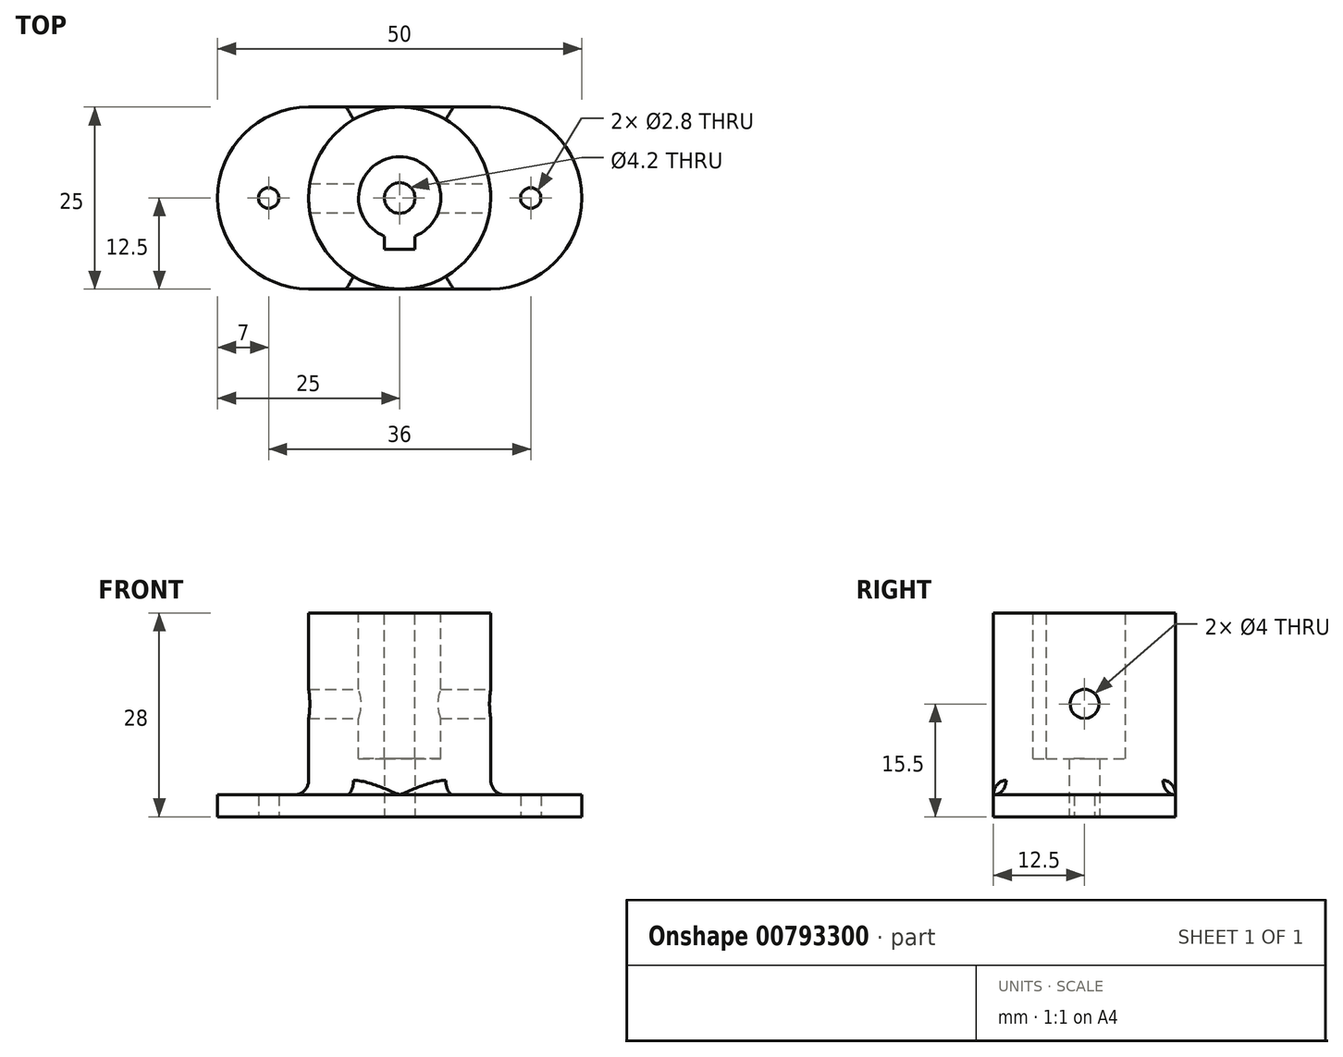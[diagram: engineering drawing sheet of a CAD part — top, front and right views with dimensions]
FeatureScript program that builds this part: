
annotation { "Feature Type Name" : "Feature", "Feature Type Description" : "" }
export const myFeature = defineFeature(function(context is Context, id is Id, definition is map)
    precondition{}
    {
        {
            var Q0;
            Q0=qCreatedBy(makeId("Top.planeOp"),FACE);
            var sketch = newSketch(context, id + "F0", { "sketchPlane" : qUnion([Q0])});
            skLineSegment(sketch, "E0.bottom", {"start": v(25, -12.5) * mm, "end": v(-25, -12.5) * mm});
            skLineSegment(sketch, "E0.top", {"start": v(25, 12.5) * mm, "end": v(-25, 12.5) * mm});
            skLineSegment(sketch, "E0.left", {"start": v(25, -12.5) * mm, "end": v(25, 12.5) * mm});
            skLineSegment(sketch, "E0.right", {"start": v(-25, -12.5) * mm, "end": v(-25, 12.5) * mm});
            skPoint(sketch, "E0.middle", {"position": v(0, 0) * mm});
            skCircle(sketch, "E1", {"center": v(-18, 0) * mm, "radius": 1.4 * mm});
            skCircle(sketch, "E2", {"center": v(18, 0) * mm, "radius": 1.4 * mm});
            skSolve(sketch);
        }
        {
            var Q0;
            Q0=qSketchRegion(id+"F0",true);
            extrude(context, id + "F1", {"entities" : qUnion([Q0]), "depth" : 3 * mm, "offsetDistance" : 25 * mm});
        }
        {
            var Q0;
            Q0=makeQuery(id+"F1.opExtrude","SWEPT_EDGE",EDGE,{"disambiguationData":[OSD([sQuery(id+"F0.wireOp",EDGE,"E0.top"),sQuery(id+"F0.wireOp",EDGE,"E0.right")])]});
            var Q1;
            Q1=makeQuery(id+"F1.opExtrude","SWEPT_EDGE",EDGE,{"disambiguationData":[OSD([sQuery(id+"F0.wireOp",EDGE,"E0.bottom"),sQuery(id+"F0.wireOp",EDGE,"E0.right")])]});
            var Q2;
            Q2=makeQuery(id+"F1.opExtrude","SWEPT_EDGE",EDGE,{"disambiguationData":[OSD([sQuery(id+"F0.wireOp",EDGE,"E0.top"),sQuery(id+"F0.wireOp",EDGE,"E0.left")])]});
            var Q3;
            Q3=makeQuery(id+"F1.opExtrude","SWEPT_EDGE",EDGE,{"disambiguationData":[OSD([sQuery(id+"F0.wireOp",EDGE,"E0.bottom"),sQuery(id+"F0.wireOp",EDGE,"E0.left")])]});
            fillet(context, id + "F2", {"entities" : qUnion([Q0, Q1, Q2, Q3]), "radius" : 12.5 * mm, "tangentPropagation" : true, "allowEdgeOverflow" : false});
        }
        {
            var Q0;
            Q0=makeQuery(id+"F1.opExtrude","CAP_FACE",FACE,{"disambiguationData":[OSD([sQuery(id+"F0.wireOp",EDGE,"E0.bottom"),sQuery(id+"F0.wireOp",EDGE,"E0.top"),sQuery(id+"F0.wireOp",EDGE,"E0.left"),sQuery(id+"F0.wireOp",EDGE,"E0.right"),sQuery(id+"F0.wireOp",EDGE,"E1"),sQuery(id+"F0.wireOp",EDGE,"E2")])],"isStart":false});
            var sketch = newSketch(context, id + "F3", { "sketchPlane" : qUnion([Q0])});
            skCircle(sketch, "E3", {"center": v(0, 0) * mm, "radius": 12.5 * mm});
            skSolve(sketch);
        }
        {
            var Q0;
            Q0 = qSketchRegion(id + "F3", true);
            extrude(context, id + "F4", {"entities" : qUnion([Q0]), "operationType" : NewBodyOperationType.ADD, "depth" : 25 * mm, "offsetDistance" : 25 * mm});
        }
        {
            var Q0;
            Q0=makeQuery(id+"F4.opExtrude","CAP_FACE",FACE,{"disambiguationData":[OSD([sQuery(id+"F3.wireOp",EDGE,"E3")])],"isStart":false});
            var sketch = newSketch(context, id + "F5", { "sketchPlane" : qUnion([Q0])});
            skArc(sketch, "E4", {"start": v(2.1, -5.25) * mm, "mid": v(0, 5.65) * mm, "end": v(-2.1, -5.25) * mm});
            skLineSegment(sketch, "E5", {"start": v(-2.1, -7.05) * mm, "end": v(2.1, -7.05) * mm});
            skLineSegment(sketch, "E6", {"start": v(-2.1, -7.05) * mm, "end": v(-2.1, -5.25) * mm});
            skLineSegment(sketch, "E7", {"start": v(2.1, -7.05) * mm, "end": v(2.1, -5.25) * mm});
            skSolve(sketch);
        }
        {
            var Q0;
            Q0 = qSketchRegion(id + "F5", true);
            extrude(context, id + "F6", {"entities" : qUnion([Q0]), "operationType" : NewBodyOperationType.REMOVE, "oppositeDirection" : true, "depth" : 20 * mm, "offsetDistance" : 25 * mm});
        }
        {
            var Q0;
            Q0=makeQuery(id+"F1.opExtrude","CAP_FACE",FACE,{"disambiguationData":[OSD([sQuery(id+"F0.wireOp",EDGE,"E0.bottom"),sQuery(id+"F0.wireOp",EDGE,"E0.top"),sQuery(id+"F0.wireOp",EDGE,"E0.left"),sQuery(id+"F0.wireOp",EDGE,"E0.right"),sQuery(id+"F0.wireOp",EDGE,"E1"),sQuery(id+"F0.wireOp",EDGE,"E2")])],"isStart":true});
            var sketch = newSketch(context, id + "F7", { "sketchPlane" : qUnion([Q0])});
            skCircle(sketch, "E8", {"center": v(0, 0) * mm, "radius": 2.1 * mm});
            skSolve(sketch);
        }
        {
            var Q0;
            Q0 = qSketchRegion(id + "F7", true);
            extrude(context, id + "F8", {"entities" : qUnion([Q0]), "operationType" : NewBodyOperationType.REMOVE, "endBound" : BoundingType.THROUGH_ALL, "oppositeDirection" : true, "depth" : 25 * mm, "offsetDistance" : 25 * mm});
        }
        {
            var Q0;
            Q0=makeQuery(id+"F4.boolean.opBoolean","SPLIT",EDGE,{"disambiguationData":[OD(1.0)],"derivedFrom":makeQuery(id+"F4.opExtrude","CAP_EDGE",EDGE,{"disambiguationData":[OSD([sQuery(id+"F3.wireOp",EDGE,"E3")])],"isStart":true})});
            fillet(context, id + "F9", {"entities" : qUnion([Q0]), "radius" : 2 * mm, "tangentPropagation" : true, "allowEdgeOverflow" : false});
        }
        {
            var Q0;
            Q0=qCreatedBy(makeId("Right.planeOp"),FACE);
            var sketch = newSketch(context, id + "F10", { "sketchPlane" : qUnion([Q0])});
            skCircle(sketch, "E9", {"center": v(0, 15.5) * mm, "radius": 2 * mm});
            skSolve(sketch);
        }
        {
            var Q0;
            Q0 = qSketchRegion(id + "F10", true);
            extrude(context, id + "F11", {"entities" : qUnion([Q0]), "operationType" : NewBodyOperationType.REMOVE, "endBound" : BoundingType.SYMMETRIC, "oppositeDirection" : true, "depth" : 100 * mm, "offsetDistance" : 25 * mm});
        }
    });
